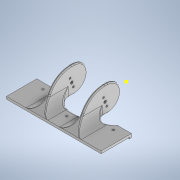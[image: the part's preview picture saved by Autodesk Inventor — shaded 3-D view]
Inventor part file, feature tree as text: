
AUTODESK INVENTOR PART (.ipt)
format: ipt  version: 2021.2 (Build 252289000, 289)  size: 1,089,536 bytes
history: native  units: in
note: dims shown in document units (in); Inventor stores cm internally (conversion verified against a paired STEP export)
features: fillet x11, sketch x9, extrude x8, reference x4, other x4, plane x3, mirror x1
ambient origin geometry x8: Origin, YZ Plane, XZ Plane, XY Plane, X Axis, Y Axis, Z Axis, Center Point
bodies: Solid1 (feature_tree)
feature tree (40):
  plane  "Work Plane1"
  extrude  "Extrusion1"  Depth=1.2748in
  plane  "Work Plane3"
  extrude  "Extrusion3"  TaperAngle=0.0deg  [1 undecoded]
  mirror  "Mirror1"
  extrude  "Extrusion4"  Depth=0.3937in TaperAngle=0.0deg
  sketch  "Sketch5"  dims[d30=0.3937in d31=0.0in d32=0.0in d33=0.0in]
  plane  "Work Plane4"
  extrude  "Extrusion5"  TaperAngle=0.0deg  [1 undecoded]
  sketch  "Sketch6"  dims[d34=1.9685in d35=1.9685in]
  extrude  "Extrusion8"  Depth=1.9685in
  extrude  "Extrusion9"  Depth=0.7874in
  extrude  "Extrusion10"  Depth=0.3937in
  fillet  "Fillet7"  Radius=0.7874in
  fillet  "Fillet8"  Radius=0.1969in
  fillet  "Fillet9"  Radius=0.0787in
  fillet  "Fillet10"  Radius=0.0118in
  fillet  "Fillet11"  Radius=0.0118in
  fillet  "Fillet12"  Radius=0.0118in
  fillet  "Fillet13"  [1 undecoded]
  fillet  "Fillet14"  [1 undecoded]
  fillet  "Fillet15"  [1 undecoded]
  fillet  "Fillet16"  [1 undecoded]
  fillet  "Fillet17"  [1 undecoded]
  extrude  "Extrusion11"  [1 undecoded]
  sketch  "Sketch1"  dims[d4=0.1969in d5=0.0in d8=1.2748in]
  reference  "Reference1"
  sketch  "Sketch3"  dims[d10=0.1969in d11=0.0in d12=0.0in d13=0.0in]
  sketch  "Sketch4"  dims[d14=0.1969in d15=0.0in d28=0.3937in d29=0.0in]
  sketch  "Sketch9"  dims[d36=0.7874in d37=0.7874in]
  sketch  "Sketch10"  dims[d38=0.3937in d39=0.1575in d40=0.7874in d41=0.1969in d42=0.0787in d43=0.0118in d44=0.0118in d45=0.0118in d46=0.0in d47=0.0in]
  reference  "Reference6"
  reference  "Reference7"
  reference  "Reference8"
  sketch  "Sketch11"
  sketch  "Sketch12"
  other  "<userpath>\Documents\Inventor\AM Research\Assembly2.iam"
  other  "Assembly2.iam"
  other  "the big cover v1:1"
  other  "USB3 WFOV:1"
note: 8 required parameter values undecoded (feature->parameter linkage not recoverable at this tier; creation-order binding heuristic only, values carry confidence <= 0.55)
